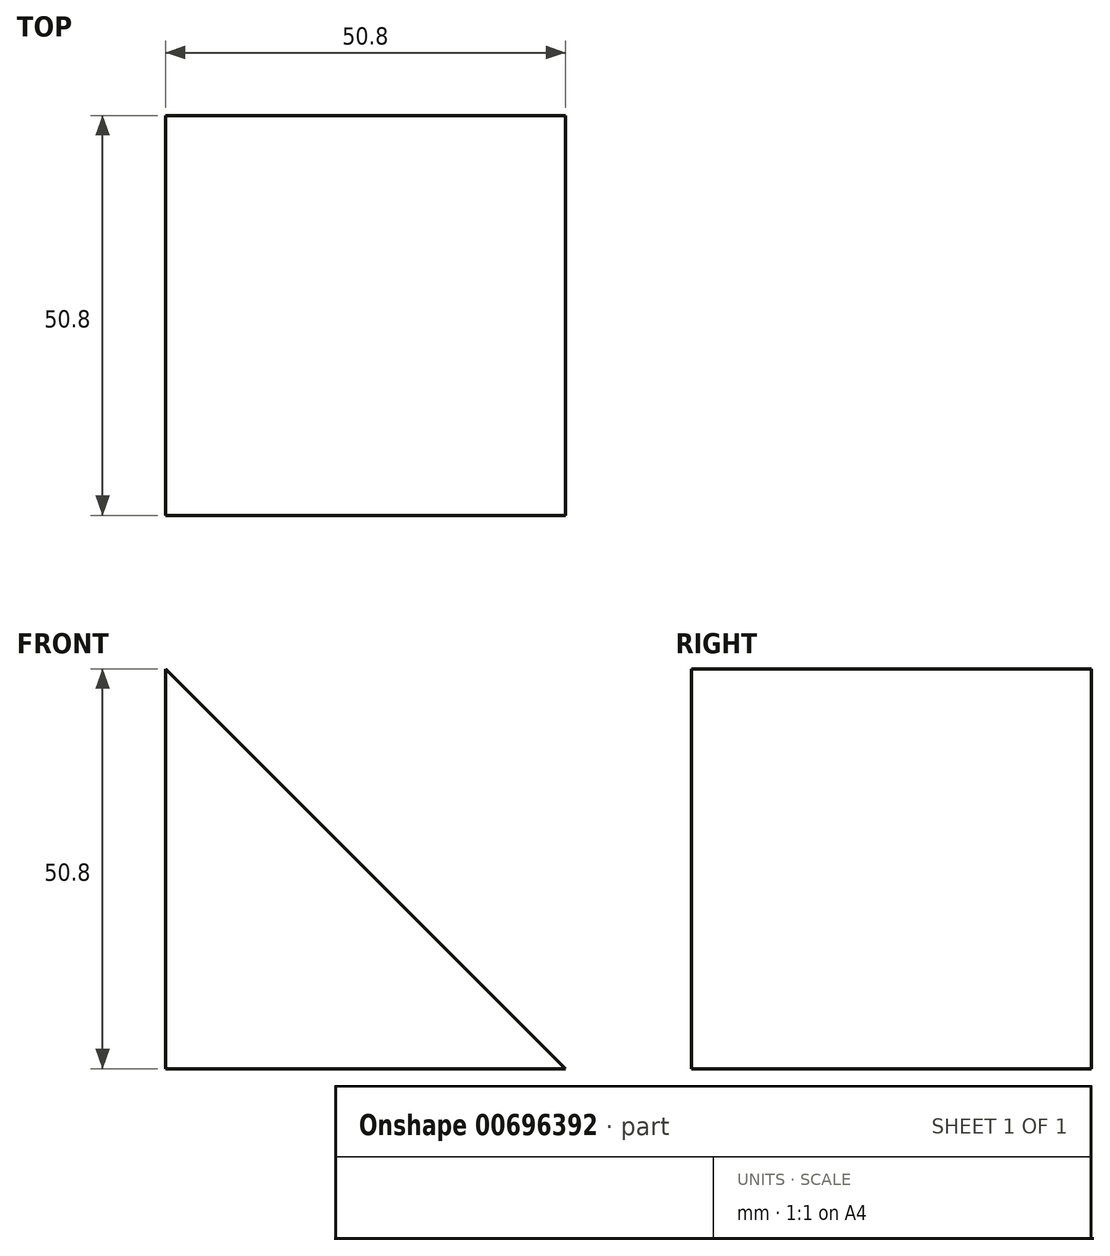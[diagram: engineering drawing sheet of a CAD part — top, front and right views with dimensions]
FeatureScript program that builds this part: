
annotation { "Feature Type Name" : "Feature", "Feature Type Description" : "" }
export const myFeature = defineFeature(function(context is Context, id is Id, definition is map)
    precondition{}
    {
        {
            var Q0;
            Q0=qCreatedBy(makeId("Front.planeOp"),FACE);
            var sketch = newSketch(context, id + "F0", { "sketchPlane" : qUnion([Q0])});
            skLineSegment(sketch, "E0.bottom", {"start": v(0, 0) * mm, "end": v(-50.8, 0) * mm});
            skLineSegment(sketch, "E0.top", {"start": v(0, 50.8) * mm, "end": v(-50.8, 50.8) * mm});
            skLineSegment(sketch, "E0.left", {"start": v(0, 0) * mm, "end": v(0, 50.8) * mm});
            skLineSegment(sketch, "E0.right", {"start": v(-50.8, 0) * mm, "end": v(-50.8, 50.8) * mm});
            skLineSegment(sketch, "E1", {"start": v(0, 0) * mm, "end": v(-50.8, 50.8) * mm});
            skSolve(sketch);
        }
        {
            var Q0;
            Q0=makeQuery(id+"F0.imprint","IMPRINT",FACE,{"disambiguationData":[TD([[makeQuery(id+"F0.imprint","IMPRINT",EDGE,{"derivedFrom":sQuery(id+"F0.wireOp",EDGE,"E0.bottom")}),-1.0]])]});
            extrude(context, id + "F1", {"entities" : qUnion([Q0]), "depth" : 50.8 * mm, "offsetDistance" : 25.4 * mm});
        }
    });
